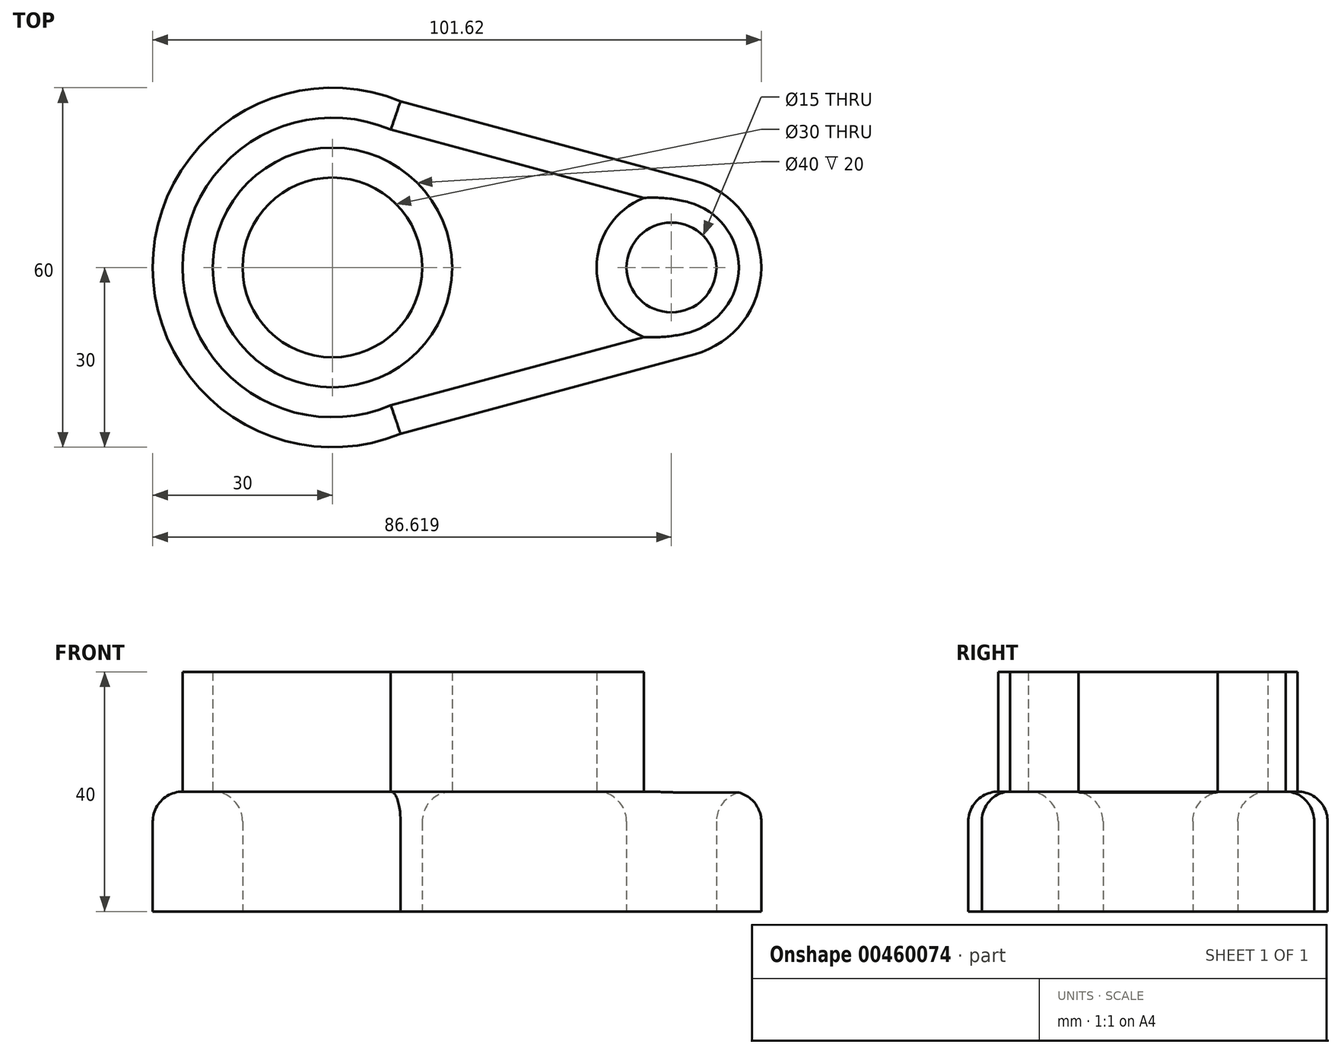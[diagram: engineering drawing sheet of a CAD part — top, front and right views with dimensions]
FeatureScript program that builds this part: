
annotation { "Feature Type Name" : "Feature", "Feature Type Description" : "" }
export const myFeature = defineFeature(function(context is Context, id is Id, definition is map)
    precondition{}
    {
        {
            var Q0;
            Q0=qCreatedBy(makeId("Top.planeOp"),FACE);
            var sketch = newSketch(context, id + "F0", { "sketchPlane" : qUnion([Q0])});
            skCircle(sketch, "E0", {"center": v(0, 0) * mm, "radius": 30 * mm});
            skCircle(sketch, "E1", {"center": v(56.62, 0) * mm, "radius": 15 * mm});
            skLineSegment(sketch, "E2", {"start": v(4.15, 29.71) * mm, "end": v(60.53, 14.48) * mm});
            skLineSegment(sketch, "E3", {"start": v(4.15, -29.71) * mm, "end": v(60.53, -14.48) * mm});
            skCircle(sketch, "E4", {"center": v(0, 0) * mm, "radius": 15 * mm});
            skCircle(sketch, "E5", {"center": v(56.62, 0) * mm, "radius": 7.5 * mm});
            skSolve(sketch);
        }
        {
            var Q0;
            Q0 = qSketchRegion(id + "F0", true);
            extrude(context, id + "F1", {"entities" : qUnion([Q0]), "depth" : 20 * mm});
        }
        {
            var Q0;
            Q0=makeQuery(id+"F1.opExtrude","CAP_FACE",FACE,{"disambiguationData":[OSD([sQuery(id+"F0.wireOp",EDGE,"E0"),sQuery(id+"F0.wireOp",EDGE,"E1"),sQuery(id+"F0.wireOp",EDGE,"E2"),sQuery(id+"F0.wireOp",EDGE,"E3"),sQuery(id+"F0.wireOp",EDGE,"E4"),sQuery(id+"F0.wireOp",EDGE,"E5")])],"isStart":false});
            fillet(context, id + "F2", {"entities" : qUnion([Q0]), "radius" : 5 * mm, "tangentPropagation" : true, "allowEdgeOverflow" : false});
        }
        {
            var Q0;
            Q0=makeQuery(id+"F1.opExtrude","CAP_FACE",FACE,{"disambiguationData":[OSD([sQuery(id+"F0.wireOp",EDGE,"E0"),sQuery(id+"F0.wireOp",EDGE,"E1"),sQuery(id+"F0.wireOp",EDGE,"E2"),sQuery(id+"F0.wireOp",EDGE,"E3"),sQuery(id+"F0.wireOp",EDGE,"E4"),sQuery(id+"F0.wireOp",EDGE,"E5")])],"isStart":false});
            extrude(context, id + "F3", {"entities" : qUnion([Q0]), "operationType" : NewBodyOperationType.ADD, "depth" : 20 * mm});
        }
        {
            var Q0;
            Q0=qCreatedBy(makeId("Top.planeOp"),FACE);
            var sketch = newSketch(context, id + "F4", { "sketchPlane" : qUnion([Q0])});
            skCircle(sketch, "E6", {"center": v(0, 47.94) * mm, "radius": 9.6 * mm});
            skSolve(sketch);
        }
        {
            var Q0;
            Q0=sQuery(id+"F4.wireOp",EDGE,"E6");
            extrude(context, id + "F5", {"bodyType" : ToolBodyType.SURFACE, "surfaceEntities" : qUnion([Q0]), "depth" : 20 * mm});
        }
    });
